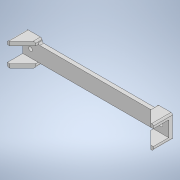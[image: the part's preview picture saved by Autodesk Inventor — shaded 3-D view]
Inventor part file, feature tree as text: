
AUTODESK INVENTOR PART (.ipt)
format: ipt  version: 2022 (Build 260153000, 153)  size: 150,528 bytes
history: native  units: mm
features: extrude x2, plane x2, mirror x2, sketch x1, hole x1, chamfer x1, fillet x1
ambient origin geometry x8: Origin, YZ Plane, XZ Plane, XY Plane, X Axis, Y Axis, Z Axis, Center Point
bodies: Solid1 (feature_tree)
feature tree (10):
  sketch  "Sketch1"  dims[d0=169.8625mm d1=20.0mm d2=10.0mm d3=10.0mm d4=10.0mm d5=5.0mm d6=0.0mm d7=5.0mm d8=6.0mm d9=6.5024mm d10=3.4036mm d11=14.3117mm d12=8.0mm d13=20.594885mm d14=20.0mm d15=5.0mm d16=25.0mm d17=0.0mm d18=16.75mm d19=2.0mm d20=45.0deg d21=2.0mm]
  extrude  "Extrusion1"  Depth=20.0mm
  hole  "Hole1"  [1 undecoded]
  extrude  "Extrusion2"  Depth=10.0mm
  plane  "Work Plane1"
  plane  "Work Plane2"
  chamfer  "Chamfer1"  Distance=10.0mm
  fillet  "Fillet1"  Radius=5.0mm
  mirror  "Mirror1"
  mirror  "Mirror2"
note: 1 required parameter value undecoded (feature->parameter linkage not recoverable at this tier; creation-order binding heuristic only, values carry confidence <= 0.55)
